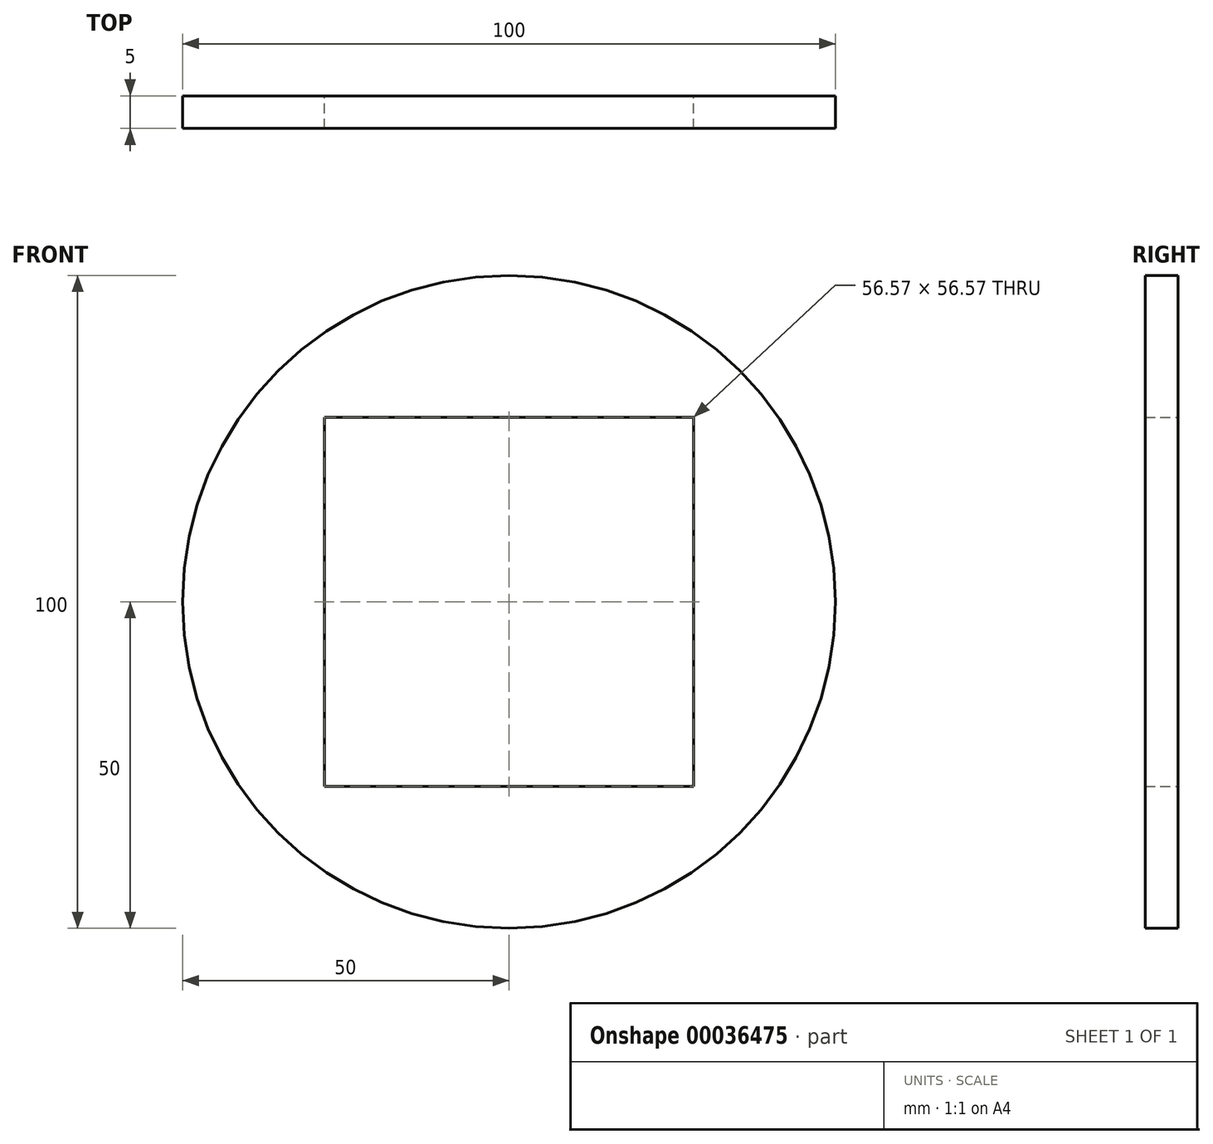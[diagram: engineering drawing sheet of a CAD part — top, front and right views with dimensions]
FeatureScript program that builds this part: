
annotation { "Feature Type Name" : "Feature", "Feature Type Description" : "" }
export const myFeature = defineFeature(function(context is Context, id is Id, definition is map)
    precondition{}
    {
        {
            var Q0;
            Q0=qCreatedBy(makeId("Front.planeOp"),FACE);
            var sketch = newSketch(context, id + "F0", { "sketchPlane" : qUnion([Q0])});
            skCircle(sketch, "E0", {"center": v(0, 0) * mm, "radius": 50 * mm});
            skCircle(sketch, "E1", {"center": v(0, 0) * mm, "radius": 40 * mm, "construction": true});
            skLineSegment(sketch, "E2.rect.bottom", {"start": v(28.28, -28.28) * mm, "end": v(-28.28, -28.28) * mm});
            skLineSegment(sketch, "E2.rect.top", {"start": v(28.28, 28.28) * mm, "end": v(-28.28, 28.28) * mm});
            skLineSegment(sketch, "E2.rect.left", {"start": v(28.28, -28.28) * mm, "end": v(28.28, 28.28) * mm});
            skLineSegment(sketch, "E2.rect.right", {"start": v(-28.28, -28.28) * mm, "end": v(-28.28, 28.28) * mm});
            skSolve(sketch);
        }
        {
            var Q0;
            Q0=makeQuery(id+"F0.imprint","IMPRINT",FACE,{"disambiguationData":[TD([[makeQuery(id+"F0.imprint","IMPRINT",EDGE,{"derivedFrom":sQuery(id+"F0.wireOp",EDGE,"E0")}),1.0]])]});
            var Q1;
            Q1=sQuery(id+"F0.wireOp",EDGE,"E1");
            extrude(context, id + "F1", {"entities" : qUnion([Q0]), "surfaceEntities" : qUnion([Q1]), "depth" : 5 * mm});
        }
    });
